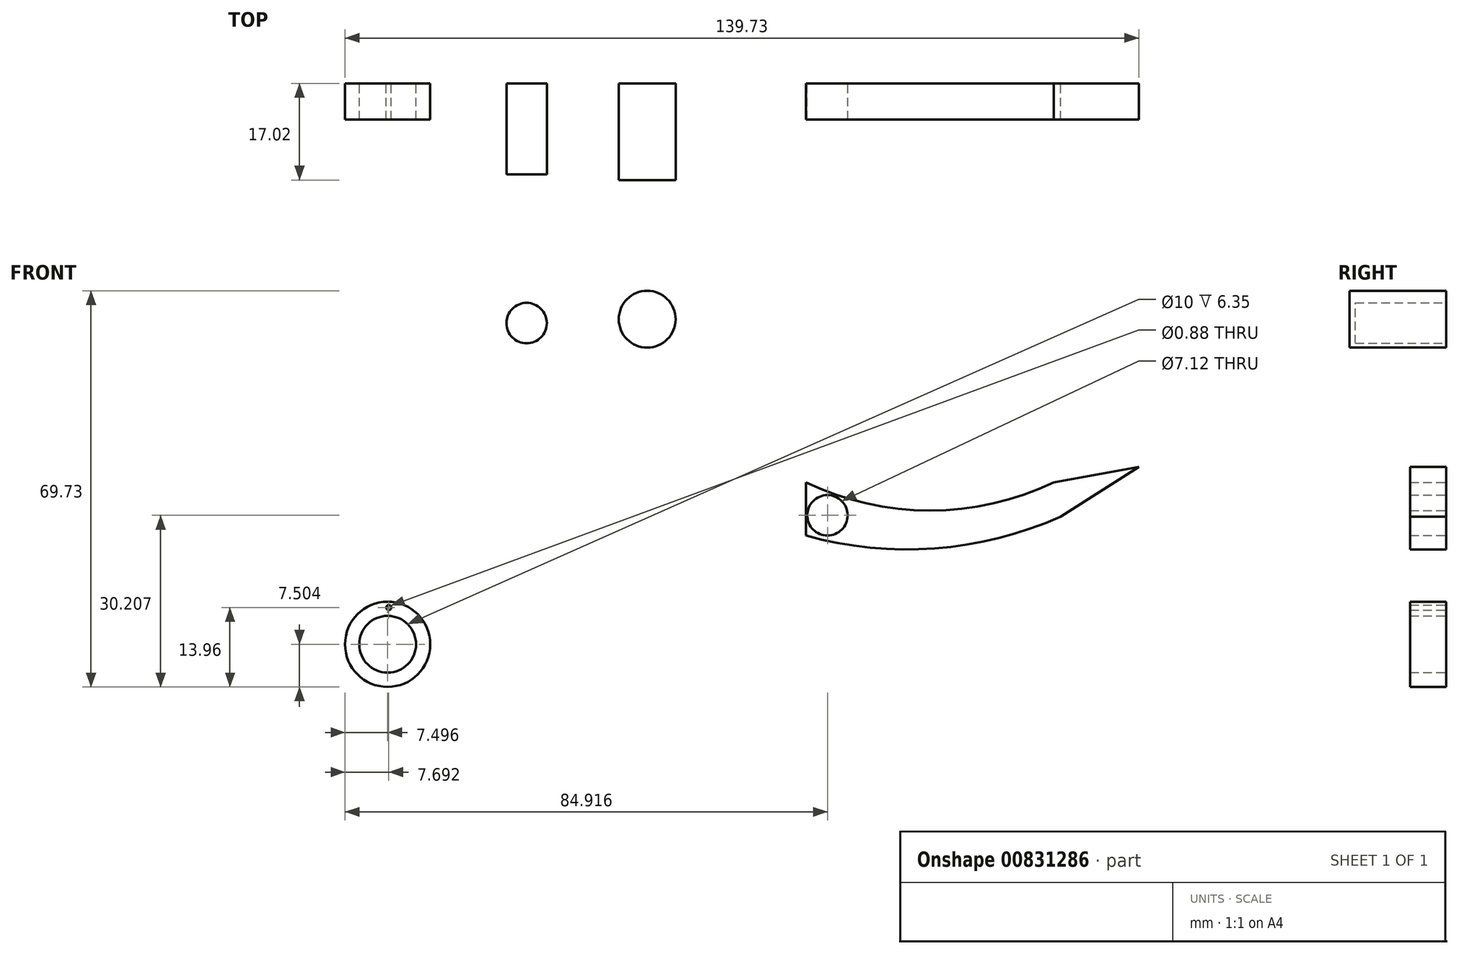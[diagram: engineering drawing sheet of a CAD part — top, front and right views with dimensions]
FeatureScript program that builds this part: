
annotation { "Feature Type Name" : "Feature", "Feature Type Description" : "" }
export const myFeature = defineFeature(function(context is Context, id is Id, definition is map)
    precondition{}
    {
        {
            var Q0;
            Q0=qCreatedBy(makeId("Front.planeOp"),FACE);
            var sketch = newSketch(context, id + "F0", { "sketchPlane" : qUnion([Q0])});
            skLineSegment(sketch, "E0", {"start": v(0, 0) * mm, "end": v(0, -9.37) * mm});
            skArc(sketch, "E1", {"start": v(0, -9.37) * mm, "mid": v(22.71, -11.63) * mm, "end": v(44.84, -6.05) * mm});
            skArc(sketch, "E2", {"start": v(0, 0) * mm, "mid": v(21.83, -4.98) * mm, "end": v(43.66, 0) * mm});
            skLineSegment(sketch, "E3", {"start": v(43.66, 0) * mm, "end": v(58.6, 2.73) * mm});
            skLineSegment(sketch, "E4", {"start": v(58.6, 2.73) * mm, "end": v(44.84, -6.05) * mm});
            skCircle(sketch, "E5", {"center": v(3.8, -5.81) * mm, "radius": 3.56 * mm});
            skCircle(sketch, "E6", {"center": v(-73.62, -28.52) * mm, "radius": 7.5 * mm});
            skCircle(sketch, "E7", {"center": v(-73.62, -28.52) * mm, "radius": 5 * mm});
            skCircle(sketch, "E8", {"center": v(-49.16, 28.03) * mm, "radius": 3.56 * mm});
            skCircle(sketch, "E9", {"center": v(-27.94, 28.7) * mm, "radius": 5 * mm});
            skCircle(sketch, "E10", {"center": v(-73.43, -22.06) * mm, "radius": 0.44 * mm});
            skSolve(sketch);
        }
        {
            var Q0;
            Q0=makeQuery(id+"F0.imprint","IMPRINT",FACE,{"disambiguationData":[TD([[makeQuery(id+"F0.imprint","IMPRINT",EDGE,{"derivedFrom":sQuery(id+"F0.wireOp",EDGE,"E0")}),1.0]])]});
            extrude(context, id + "F1", {"entities" : qUnion([Q0]), "depth" : 6.35 * mm, "offsetDistance" : 25.4 * mm});
        }
        {
            var Q0;
            Q0=makeQuery(id+"F0.imprint","IMPRINT",FACE,{"disambiguationData":[TD([[makeQuery(id+"F0.imprint","IMPRINT",EDGE,{"derivedFrom":sQuery(id+"F0.wireOp",EDGE,"E8")}),1.0]])]});
            var Q1;
            Q1=makeQuery(id+"F0.imprint","IMPRINT",FACE,{"disambiguationData":[TD([[makeQuery(id+"F0.imprint","IMPRINT",EDGE,{"derivedFrom":sQuery(id+"F0.wireOp",EDGE,"E6")}),1.0]])]});
            extrude(context, id + "F2", {"entities" : qUnion([Q0, Q1]), "depth" : 6.35 * mm, "offsetDistance" : 25.4 * mm});
        }
        {
            var Q0;
            Q0=makeQuery(id+"F0.imprint","IMPRINT",FACE,{"disambiguationData":[TD([[makeQuery(id+"F0.imprint","IMPRINT",EDGE,{"derivedFrom":sQuery(id+"F0.wireOp",EDGE,"E8")}),1.0]])]});
            extrude(context, id + "F3", {"entities" : qUnion([Q0]), "operationType" : NewBodyOperationType.ADD, "depth" : 16 * mm, "offsetDistance" : 25.4 * mm});
        }
        {
            var Q0;
            Q0=makeQuery(id+"F0.imprint","IMPRINT",FACE,{"disambiguationData":[TD([[makeQuery(id+"F0.imprint","IMPRINT",EDGE,{"derivedFrom":sQuery(id+"F0.wireOp",EDGE,"E9")}),1.0]])]});
            extrude(context, id + "F4", {"entities" : qUnion([Q0]), "depth" : 17.02 * mm, "offsetDistance" : 25.4 * mm});
        }
    });
